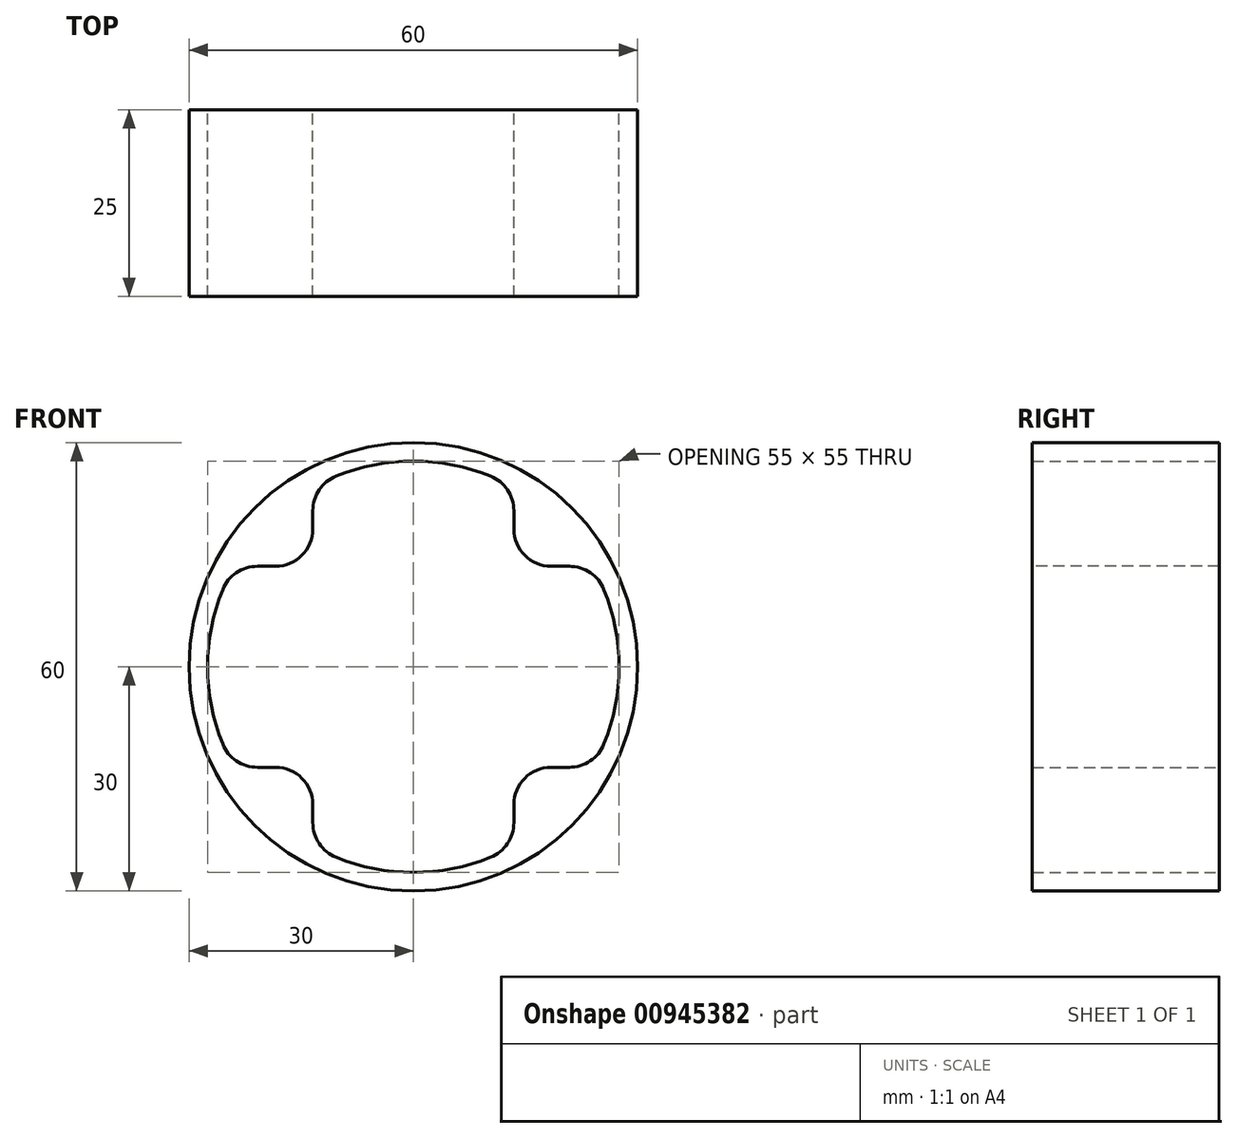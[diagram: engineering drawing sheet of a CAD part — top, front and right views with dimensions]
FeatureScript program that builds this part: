
annotation { "Feature Type Name" : "Feature", "Feature Type Description" : "" }
export const myFeature = defineFeature(function(context is Context, id is Id, definition is map)
    precondition{}
    {
        {
            var Q0;
            Q0=qCreatedBy(makeId("Front.planeOp"),FACE);
            var sketch = newSketch(context, id + "F0", { "sketchPlane" : qUnion([Q0])});
            skCircle(sketch, "E0", {"center": v(0, 0) * mm, "radius": 30 * mm});
            skCircle(sketch, "E1", {"center": v(0, 0) * mm, "radius": 27.5 * mm});
            skSolve(sketch);
        }
        {
            var Q0;
            Q0=makeQuery(id+"F0.imprint","IMPRINT",FACE,{"disambiguationData":[TD([[makeQuery(id+"F0.imprint","IMPRINT",EDGE,{"derivedFrom":sQuery(id+"F0.wireOp",EDGE,"E0")}),1.0]])]});
            extrude(context, id + "F1", {"entities" : qUnion([Q0]), "depth" : 25 * mm, "offsetDistance" : 25 * mm});
        }
        {
            var Q0;
            Q0=qCreatedBy(makeId("Front.planeOp"),FACE);
            var sketch = newSketch(context, id + "F2", { "sketchPlane" : qUnion([Q0])});
            skLineSegment(sketch, "E2", {"start": v(0, 0) * mm, "end": v(-24.44, 24.44) * mm, "construction": true});
            skLineSegment(sketch, "E3.bottom", {"start": v(-18.44, 13.44) * mm, "end": v(-24.44, 13.44) * mm});
            skLineSegment(sketch, "E3.top", {"start": v(-13.44, 24.44) * mm, "end": v(-24.44, 24.44) * mm, "construction": true});
            skLineSegment(sketch, "E3.left", {"start": v(-13.44, 18.44) * mm, "end": v(-13.44, 24.44) * mm});
            skLineSegment(sketch, "E3.right", {"start": v(-24.44, 13.44) * mm, "end": v(-24.44, 23.44) * mm, "construction": true});
            skPoint(sketch, "E4.visualSharp", {"position": v(-13.44, 13.44) * mm});
            skArc(sketch, "E4.filletArc", {"start": v(-18.44, 13.44) * mm, "mid": v(-14.9, 14.9) * mm, "end": v(-13.44, 18.44) * mm});
            skLineSegment(sketch, "E5.MirrorCS", {"start": v(13.44, 24.44) * mm, "end": v(24.44, 24.44) * mm, "construction": true});
            skLineSegment(sketch, "E6.MirrorCS", {"start": v(24.44, 13.44) * mm, "end": v(24.44, 23.44) * mm, "construction": true});
            skLineSegment(sketch, "E7.MirrorCS", {"start": v(18.44, 13.44) * mm, "end": v(24.44, 13.44) * mm});
            skArc(sketch, "E8.MirrorCS", {"start": v(18.44, 13.44) * mm, "mid": v(14.9, 14.9) * mm, "end": v(13.44, 18.44) * mm});
            skLineSegment(sketch, "E9.MirrorCS", {"start": v(13.44, 18.44) * mm, "end": v(13.44, 24.44) * mm});
            skLineSegment(sketch, "E10.MirrorCS", {"start": v(-24.44, -13.44) * mm, "end": v(-24.44, -23.44) * mm, "construction": true});
            skLineSegment(sketch, "E11.MirrorCS", {"start": v(-13.44, -18.44) * mm, "end": v(-13.44, -24.44) * mm});
            skArc(sketch, "E12.MirrorCS", {"start": v(-18.44, -13.44) * mm, "mid": v(-14.9, -14.9) * mm, "end": v(-13.44, -18.44) * mm});
            skLineSegment(sketch, "E13.MirrorCS", {"start": v(-18.44, -13.44) * mm, "end": v(-24.44, -13.44) * mm});
            skLineSegment(sketch, "E14.MirrorCS", {"start": v(13.44, -18.44) * mm, "end": v(13.44, -24.44) * mm});
            skLineSegment(sketch, "E15.MirrorCS", {"start": v(13.44, -24.44) * mm, "end": v(24.44, -24.44) * mm, "construction": true});
            skLineSegment(sketch, "E16.MirrorCS", {"start": v(24.44, -13.44) * mm, "end": v(24.44, -23.44) * mm, "construction": true});
            skLineSegment(sketch, "E17.MirrorCS", {"start": v(18.44, -13.44) * mm, "end": v(24.44, -13.44) * mm});
            skArc(sketch, "E18.MirrorCS", {"start": v(18.44, -13.44) * mm, "mid": v(14.9, -14.9) * mm, "end": v(13.44, -18.44) * mm});
            skLineSegment(sketch, "E19.MirrorCS", {"start": v(-13.44, -24.44) * mm, "end": v(-24.44, -24.44) * mm, "construction": true});
            skArc(sketch, "E20", {"start": v(-13.44, 24.44) * mm, "mid": v(-19.72, 19.72) * mm, "end": v(-24.44, 13.44) * mm});
            skArc(sketch, "E21.MirrorCS", {"start": v(13.44, 24.44) * mm, "mid": v(19.72, 19.72) * mm, "end": v(24.44, 13.44) * mm});
            skArc(sketch, "E22.MirrorCS", {"start": v(-13.44, -24.44) * mm, "mid": v(-19.72, -19.72) * mm, "end": v(-24.44, -13.44) * mm});
            skArc(sketch, "E23.MirrorCS", {"start": v(13.44, -24.44) * mm, "mid": v(19.72, -19.72) * mm, "end": v(24.44, -13.44) * mm});
            skSolve(sketch);
        }
        {
            var Q0;
            Q0=makeQuery(id+"F2.imprint","IMPRINT",FACE,{"disambiguationData":[TD([[makeQuery(id+"F2.imprint","IMPRINT",EDGE,{"derivedFrom":sQuery(id+"F2.wireOp",EDGE,"E3.bottom")}),-1.0]])]});
            var Q1;
            Q1=makeQuery(id+"F2.imprint","IMPRINT",FACE,{"disambiguationData":[TD([[makeQuery(id+"F2.imprint","IMPRINT",EDGE,{"derivedFrom":sQuery(id+"F2.wireOp",EDGE,"E5.MirrorCS")}),-1.0]])]});
            var Q2;
            Q2=makeQuery(id+"F2.imprint","IMPRINT",FACE,{"disambiguationData":[TD([[makeQuery(id+"F2.imprint","IMPRINT",EDGE,{"derivedFrom":sQuery(id+"F2.wireOp",EDGE,"E10.MirrorCS")}),1.0]])]});
            var Q3;
            Q3=makeQuery(id+"F2.imprint","IMPRINT",FACE,{"disambiguationData":[TD([[makeQuery(id+"F2.imprint","IMPRINT",EDGE,{"derivedFrom":sQuery(id+"F2.wireOp",EDGE,"E14.MirrorCS")}),1.0]])]});
            var Q4;
            Q4=makeQuery(id+"F2.imprint","IMPRINT",FACE,{"disambiguationData":[TD([[makeQuery(id+"F2.imprint","IMPRINT",EDGE,{"derivedFrom":sQuery(id+"F2.wireOp",EDGE,"E7.MirrorCS")}),1.0]])]});
            var Q5;
            Q5=makeQuery(id+"F2.imprint","IMPRINT",FACE,{"disambiguationData":[TD([[makeQuery(id+"F2.imprint","IMPRINT",EDGE,{"derivedFrom":sQuery(id+"F2.wireOp",EDGE,"E11.MirrorCS")}),-1.0]])]});
            extrude(context, id + "F3", {"entities" : qUnion([Q0, Q1, Q2, Q3, Q4, Q5]), "operationType" : NewBodyOperationType.ADD, "depth" : 25 * mm, "offsetDistance" : 25 * mm});
        }
        {
            var Q0;
            Q0=makeQuery(id+"F3.boolean.opBoolean","INTERSECT",EDGE,{"derivedFrom":[makeQuery(id+"F1.opExtrude","SWEPT_FACE",FACE,{"disambiguationData":[OSD([sQuery(id+"F0.wireOp",EDGE,"E1")])]}),makeQuery(id+"F3.opExtrude","SWEPT_FACE",FACE,{"disambiguationData":[OSD([sQuery(id+"F2.wireOp",EDGE,"E3.left")])]})]});
            var Q1;
            Q1=makeQuery(id+"F3.boolean.opBoolean","INTERSECT",EDGE,{"derivedFrom":[makeQuery(id+"F1.opExtrude","SWEPT_FACE",FACE,{"disambiguationData":[OSD([sQuery(id+"F0.wireOp",EDGE,"E1")])]}),makeQuery(id+"F3.opExtrude","SWEPT_FACE",FACE,{"disambiguationData":[OSD([sQuery(id+"F2.wireOp",EDGE,"E3.bottom")])]})]});
            var Q2;
            Q2=makeQuery(id+"F3.boolean.opBoolean","INTERSECT",EDGE,{"derivedFrom":[makeQuery(id+"F1.opExtrude","SWEPT_FACE",FACE,{"disambiguationData":[OSD([sQuery(id+"F0.wireOp",EDGE,"E1")])]}),makeQuery(id+"F3.opExtrude","SWEPT_FACE",FACE,{"disambiguationData":[OSD([sQuery(id+"F2.wireOp",EDGE,"E13.MirrorCS")])]})]});
            var Q3;
            Q3=makeQuery(id+"F3.boolean.opBoolean","INTERSECT",EDGE,{"derivedFrom":[makeQuery(id+"F1.opExtrude","SWEPT_FACE",FACE,{"disambiguationData":[OSD([sQuery(id+"F0.wireOp",EDGE,"E1")])]}),makeQuery(id+"F3.opExtrude","SWEPT_FACE",FACE,{"disambiguationData":[OSD([sQuery(id+"F2.wireOp",EDGE,"E11.MirrorCS")])]})]});
            var Q4;
            Q4=makeQuery(id+"F3.boolean.opBoolean","INTERSECT",EDGE,{"derivedFrom":[makeQuery(id+"F1.opExtrude","SWEPT_FACE",FACE,{"disambiguationData":[OSD([sQuery(id+"F0.wireOp",EDGE,"E1")])]}),makeQuery(id+"F3.opExtrude","SWEPT_FACE",FACE,{"disambiguationData":[OSD([sQuery(id+"F2.wireOp",EDGE,"E9.MirrorCS")])]})]});
            var Q5;
            Q5=makeQuery(id+"F3.boolean.opBoolean","INTERSECT",EDGE,{"derivedFrom":[makeQuery(id+"F1.opExtrude","SWEPT_FACE",FACE,{"disambiguationData":[OSD([sQuery(id+"F0.wireOp",EDGE,"E1")])]}),makeQuery(id+"F3.opExtrude","SWEPT_FACE",FACE,{"disambiguationData":[OSD([sQuery(id+"F2.wireOp",EDGE,"E7.MirrorCS")])]})]});
            var Q6;
            Q6=makeQuery(id+"F3.boolean.opBoolean","INTERSECT",EDGE,{"derivedFrom":[makeQuery(id+"F1.opExtrude","SWEPT_FACE",FACE,{"disambiguationData":[OSD([sQuery(id+"F0.wireOp",EDGE,"E1")])]}),makeQuery(id+"F3.opExtrude","SWEPT_FACE",FACE,{"disambiguationData":[OSD([sQuery(id+"F2.wireOp",EDGE,"E14.MirrorCS")])]})]});
            var Q7;
            Q7=makeQuery(id+"F3.boolean.opBoolean","INTERSECT",EDGE,{"derivedFrom":[makeQuery(id+"F1.opExtrude","SWEPT_FACE",FACE,{"disambiguationData":[OSD([sQuery(id+"F0.wireOp",EDGE,"E1")])]}),makeQuery(id+"F3.opExtrude","SWEPT_FACE",FACE,{"disambiguationData":[OSD([sQuery(id+"F2.wireOp",EDGE,"E17.MirrorCS")])]})]});
            fillet(context, id + "F4", {"entities" : qUnion([Q0, Q1, Q2, Q3, Q4, Q5, Q6, Q7]), "radius" : 5 * mm, "tangentPropagation" : true, "allowEdgeOverflow" : false});
        }
    });
